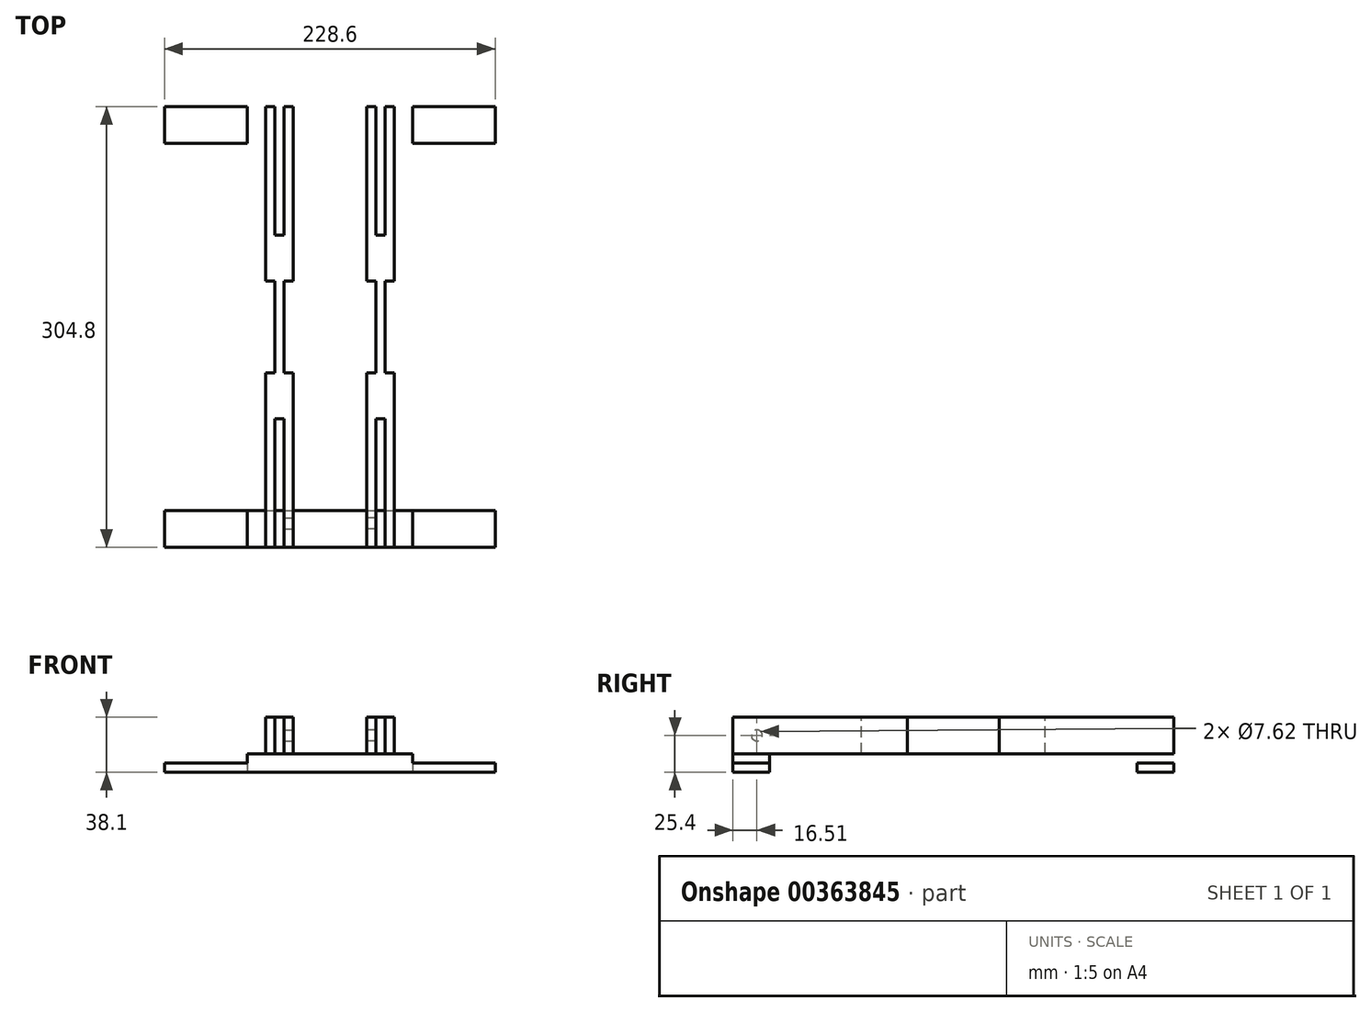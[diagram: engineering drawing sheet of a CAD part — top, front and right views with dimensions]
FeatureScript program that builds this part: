
annotation { "Feature Type Name" : "Feature", "Feature Type Description" : "" }
export const myFeature = defineFeature(function(context is Context, id is Id, definition is map)
    precondition{}
    {
        {
            var Q0;
            Q0=qCreatedBy(makeId("Top.planeOp"),FACE);
            var sketch = newSketch(context, id + "F0", { "sketchPlane" : qUnion([Q0])});
            skLineSegment(sketch, "E0.bottom", {"start": v(-114.3, 152.4) * mm, "end": v(114.3, 152.4) * mm});
            skLineSegment(sketch, "E0.top", {"start": v(-114.3, 127) * mm, "end": v(114.3, 127) * mm});
            skLineSegment(sketch, "E0.left", {"start": v(-114.3, 152.4) * mm, "end": v(-114.3, 127) * mm});
            skLineSegment(sketch, "E0.right", {"start": v(114.3, 152.4) * mm, "end": v(114.3, 127) * mm});
            skLineSegment(sketch, "E1", {"start": v(-113.97, 0) * mm, "end": v(125.77, 0) * mm});
            skLineSegment(sketch, "E2.MirrorCS", {"start": v(-114.3, -152.4) * mm, "end": v(114.3, -152.4) * mm});
            skLineSegment(sketch, "E3.MirrorCS", {"start": v(-114.3, -152.4) * mm, "end": v(-114.3, -127) * mm});
            skLineSegment(sketch, "E4.MirrorCS", {"start": v(-114.3, -127) * mm, "end": v(114.3, -127) * mm});
            skLineSegment(sketch, "E5.MirrorCS", {"start": v(114.3, -152.4) * mm, "end": v(114.3, -127) * mm});
            skLineSegment(sketch, "E6.bottom", {"start": v(-57.15, 152.4) * mm, "end": v(57.15, 152.4) * mm});
            skLineSegment(sketch, "E6.top", {"start": v(-57.15, 127) * mm, "end": v(57.15, 127) * mm});
            skLineSegment(sketch, "E6.left", {"start": v(-57.15, 152.4) * mm, "end": v(-57.15, 127) * mm});
            skLineSegment(sketch, "E6.right", {"start": v(57.15, 152.4) * mm, "end": v(57.15, 127) * mm});
            skLineSegment(sketch, "E7.MirrorCS", {"start": v(-57.15, -127) * mm, "end": v(57.15, -127) * mm});
            skLineSegment(sketch, "E8.MirrorCS", {"start": v(-57.15, -152.4) * mm, "end": v(-57.15, -127) * mm});
            skLineSegment(sketch, "E9.MirrorCS", {"start": v(57.15, -152.4) * mm, "end": v(57.15, -127) * mm});
            skLineSegment(sketch, "E10.MirrorCS", {"start": v(-57.15, -152.4) * mm, "end": v(57.15, -152.4) * mm});
            skLineSegment(sketch, "E11", {"start": v(0, 0) * mm, "end": v(0, -127) * mm});
            skSolve(sketch);
        }
        {
            var Q0;
            {var subQ0=sQuery(id+"F0.wireOp",EDGE,"E5.MirrorCS");Q0=makeQuery(id+"F0.imprint","IMPRINT",FACE,{"disambiguationData":[TD([[makeQuery(id+"F0.imprint","IMPRINT",EDGE,{"derivedFrom":subQ0}),1.0]])]});}
            var Q1;
            {var subQ0=sQuery(id+"F0.wireOp",EDGE,"E3.MirrorCS");Q1=makeQuery(id+"F0.imprint","IMPRINT",FACE,{"disambiguationData":[TD([[makeQuery(id+"F0.imprint","IMPRINT",EDGE,{"derivedFrom":subQ0}),-1.0]])]});}
            var Q2;
            {var subQ0=sQuery(id+"F0.wireOp",EDGE,"E0.left");Q2=makeQuery(id+"F0.imprint","IMPRINT",FACE,{"disambiguationData":[TD([[makeQuery(id+"F0.imprint","IMPRINT",EDGE,{"derivedFrom":subQ0}),1.0]])]});}
            var Q3;
            {var subQ0=sQuery(id+"F0.wireOp",EDGE,"E0.right");Q3=makeQuery(id+"F0.imprint","IMPRINT",FACE,{"disambiguationData":[TD([[makeQuery(id+"F0.imprint","IMPRINT",EDGE,{"derivedFrom":subQ0}),-1.0]])]});}
            extrude(context, id + "F1", {"entities" : qUnion([Q0, Q1, Q2, Q3]), "depth" : 6.35 * mm});
        }
        {
            var Q0;
            Q0=makeQuery(id+"F0.imprint","IMPRINT",FACE,{"disambiguationData":[TD([[makeQuery(id+"F0.imprint","IMPRINT",EDGE,{"derivedFrom":sQuery(id+"F0.wireOp",EDGE,"E8.MirrorCS")}),-1.0]])]});
            var Q1;
            Q1=makeQuery(id+"F0.imprint","IMPRINT",FACE,{"disambiguationData":[TD([[makeQuery(id+"F0.imprint","IMPRINT",EDGE,{"derivedFrom":sQuery(id+"F0.wireOp",EDGE,"E6.bottom")}),-1.0]])]});
            extrude(context, id + "F2", {"entities" : qUnion([Q0, Q1]), "depth" : 12.7 * mm});
        }
        {
            var Q0;
            Q0=makeQuery(id+"F1.opExtrude","SWEPT_BODY",BODY,{"disambiguationData":[OSD([sQuery(id+"F0.wireOp",EDGE,"E0.bottom"),sQuery(id+"F0.wireOp",EDGE,"E0.top"),sQuery(id+"F0.wireOp",EDGE,"E0.left"),sQuery(id+"F0.wireOp",EDGE,"E6.left")])]});
            var Q1;
            Q1=makeQuery(id+"F1.opExtrude","SWEPT_BODY",BODY,{"disambiguationData":[OSD([sQuery(id+"F0.wireOp",EDGE,"E0.bottom"),sQuery(id+"F0.wireOp",EDGE,"E0.top"),sQuery(id+"F0.wireOp",EDGE,"E0.right"),sQuery(id+"F0.wireOp",EDGE,"E6.right")])]});
            var Q2;
            Q2=makeQuery(id+"F1.opExtrude","SWEPT_BODY",BODY,{"disambiguationData":[OSD([sQuery(id+"F0.wireOp",EDGE,"E2.MirrorCS"),sQuery(id+"F0.wireOp",EDGE,"E3.MirrorCS"),sQuery(id+"F0.wireOp",EDGE,"E4.MirrorCS"),sQuery(id+"F0.wireOp",EDGE,"E8.MirrorCS")])]});
            var Q3;
            Q3=makeQuery(id+"F1.opExtrude","SWEPT_BODY",BODY,{"disambiguationData":[OSD([sQuery(id+"F0.wireOp",EDGE,"E2.MirrorCS"),sQuery(id+"F0.wireOp",EDGE,"E4.MirrorCS"),sQuery(id+"F0.wireOp",EDGE,"E5.MirrorCS"),sQuery(id+"F0.wireOp",EDGE,"E9.MirrorCS")])]});
            var Q4;
            Q4=makeQuery(id+"F2.opExtrude","SWEPT_BODY",BODY,{"disambiguationData":[OSD([sQuery(id+"F0.wireOp",EDGE,"E6.bottom"),sQuery(id+"F0.wireOp",EDGE,"E6.top"),sQuery(id+"F0.wireOp",EDGE,"E6.left"),sQuery(id+"F0.wireOp",EDGE,"E6.right")])]});
            var Q5;
            Q5=makeQuery(id+"F2.opExtrude","SWEPT_BODY",BODY,{"disambiguationData":[OSD([sQuery(id+"F0.wireOp",EDGE,"E8.MirrorCS"),sQuery(id+"F0.wireOp",EDGE,"E9.MirrorCS"),sQuery(id+"F0.wireOp",EDGE,"E10.MirrorCS"),sQuery(id+"F0.wireOp",EDGE,"E7.MirrorCS")])]});
            booleanBodies(context, id + "F3", {"operationType" : BooleanOperationType.UNION, "tools" : qUnion([Q0, Q1, Q2, Q3, Q4, Q5])});
        }
        {
            var Q0;
            {var subQ0=sQuery(id+"F0.wireOp",EDGE,"E10.MirrorCS");var subQ1=sQuery(id+"F0.wireOp",EDGE,"E2.MirrorCS");Q0=makeQuery(id+"F3.opBoolean","MERGE",FACE,{"derivedFrom":[makeQuery(id+"F1.opExtrude","SWEPT_FACE",FACE,{"disambiguationData":[OSD([subQ1]),TDD([makeQuery(id+"F0.imprint","IMPRINT",EDGE,{"disambiguationData":[TD([[makeQuery(id+"F0.imprint","INTERSECT",VERTEX,{"derivedFrom":[subQ1,sQuery(id+"F0.wireOp",EDGE,"E3.MirrorCS")]}),-1.0]])],"derivedFrom":subQ1})])]}),makeQuery(id+"F1.opExtrude","SWEPT_FACE",FACE,{"disambiguationData":[OSD([subQ1]),TDD([makeQuery(id+"F0.imprint","IMPRINT",EDGE,{"disambiguationData":[TD([[makeQuery(id+"F0.imprint","INTERSECT",VERTEX,{"derivedFrom":[subQ1,sQuery(id+"F0.wireOp",EDGE,"E5.MirrorCS")]}),1.0]])],"derivedFrom":subQ1})])]}),makeQuery(id+"F2.opExtrude","SWEPT_FACE",FACE,{"disambiguationData":[OSD([subQ0])]})]});}
            var sketch = newSketch(context, id + "F4", { "sketchPlane" : qUnion([Q0])});
            skLineSegment(sketch, "E12", {"start": v(0, 59.29) * mm, "end": v(0, 0) * mm});
            skLineSegment(sketch, "E13.bottom", {"start": v(-44.45, 12.7) * mm, "end": v(-38.1, 12.7) * mm});
            skLineSegment(sketch, "E13.top", {"start": v(-44.45, 38.1) * mm, "end": v(-38.1, 38.1) * mm});
            skLineSegment(sketch, "E13.left", {"start": v(-44.45, 12.7) * mm, "end": v(-44.45, 38.1) * mm});
            skLineSegment(sketch, "E13.right", {"start": v(-38.1, 12.7) * mm, "end": v(-38.1, 38.1) * mm});
            skLineSegment(sketch, "E14.bottom", {"start": v(-31.75, 12.7) * mm, "end": v(-25.4, 12.7) * mm});
            skLineSegment(sketch, "E14.top", {"start": v(-31.75, 38.1) * mm, "end": v(-25.4, 38.1) * mm});
            skLineSegment(sketch, "E14.left", {"start": v(-31.75, 12.7) * mm, "end": v(-31.75, 38.1) * mm});
            skLineSegment(sketch, "E14.right", {"start": v(-25.4, 12.7) * mm, "end": v(-25.4, 38.1) * mm});
            skLineSegment(sketch, "E15.MirrorCS", {"start": v(25.4, 12.7) * mm, "end": v(25.4, 38.1) * mm});
            skLineSegment(sketch, "E16.MirrorCS", {"start": v(31.75, 38.1) * mm, "end": v(25.4, 38.1) * mm});
            skLineSegment(sketch, "E17.MirrorCS", {"start": v(31.75, 12.7) * mm, "end": v(25.4, 12.7) * mm});
            skLineSegment(sketch, "E18.MirrorCS", {"start": v(31.75, 12.7) * mm, "end": v(31.75, 38.1) * mm});
            skLineSegment(sketch, "E19.MirrorCS", {"start": v(38.1, 12.7) * mm, "end": v(38.1, 38.1) * mm});
            skLineSegment(sketch, "E20.MirrorCS", {"start": v(44.45, 12.7) * mm, "end": v(44.45, 38.1) * mm});
            skLineSegment(sketch, "E21.MirrorCS", {"start": v(44.45, 38.1) * mm, "end": v(38.1, 38.1) * mm});
            skLineSegment(sketch, "E22.MirrorCS", {"start": v(44.45, 12.7) * mm, "end": v(38.1, 12.7) * mm});
            skLineSegment(sketch, "E23.bottom", {"start": v(-38.1, 38.1) * mm, "end": v(-31.75, 38.1) * mm});
            skLineSegment(sketch, "E23.top", {"start": v(-38.1, 12.7) * mm, "end": v(-31.75, 12.7) * mm});
            skLineSegment(sketch, "E23.left", {"start": v(-38.1, 38.1) * mm, "end": v(-38.1, 12.7) * mm});
            skLineSegment(sketch, "E23.right", {"start": v(-31.75, 38.1) * mm, "end": v(-31.75, 12.7) * mm});
            skLineSegment(sketch, "E24.bottom", {"start": v(31.75, 38.1) * mm, "end": v(38.1, 38.1) * mm});
            skLineSegment(sketch, "E24.top", {"start": v(31.75, 12.7) * mm, "end": v(38.1, 12.7) * mm});
            skLineSegment(sketch, "E24.left", {"start": v(31.75, 38.1) * mm, "end": v(31.75, 12.7) * mm});
            skLineSegment(sketch, "E24.right", {"start": v(38.1, 38.1) * mm, "end": v(38.1, 12.7) * mm});
            skSolve(sketch);
        }
        {
            var Q0;
            Q0=makeQuery(id+"F4.imprint","IMPRINT",FACE,{"disambiguationData":[TD([[makeQuery(id+"F4.imprint","IMPRINT",EDGE,{"derivedFrom":sQuery(id+"F4.wireOp",EDGE,"E13.bottom")}),1.0]])]});
            var Q1;
            Q1=makeQuery(id+"F4.imprint","IMPRINT",FACE,{"disambiguationData":[TD([[makeQuery(id+"F4.imprint","IMPRINT",EDGE,{"derivedFrom":sQuery(id+"F4.wireOp",EDGE,"E14.bottom")}),1.0]])]});
            var Q2;
            Q2=makeQuery(id+"F4.imprint","IMPRINT",FACE,{"disambiguationData":[TD([[makeQuery(id+"F4.imprint","IMPRINT",EDGE,{"derivedFrom":sQuery(id+"F4.wireOp",EDGE,"E19.MirrorCS")}),-1.0]])]});
            var Q3;
            Q3=makeQuery(id+"F4.imprint","IMPRINT",FACE,{"disambiguationData":[TD([[makeQuery(id+"F4.imprint","IMPRINT",EDGE,{"derivedFrom":sQuery(id+"F4.wireOp",EDGE,"E23.bottom")}),-1.0]])]});
            var Q4;
            Q4=makeQuery(id+"F4.imprint","IMPRINT",FACE,{"disambiguationData":[TD([[makeQuery(id+"F4.imprint","IMPRINT",EDGE,{"derivedFrom":sQuery(id+"F4.wireOp",EDGE,"E15.MirrorCS")}),-1.0]])]});
            var Q5;
            Q5=makeQuery(id+"F4.imprint","IMPRINT",FACE,{"disambiguationData":[TD([[makeQuery(id+"F4.imprint","IMPRINT",EDGE,{"derivedFrom":sQuery(id+"F4.wireOp",EDGE,"E24.bottom")}),-1.0]])]});
            var Q6;
            Q6=makeQuery(id+"F4.imprint","IMPRINT",FACE,{"disambiguationData":[TD([[makeQuery(id+"F4.imprint","IMPRINT",EDGE,{"derivedFrom":sQuery(id+"F4.wireOp",EDGE,"E20.MirrorCS")}),1.0]])]});
            extrude(context, id + "F5", {"entities" : qUnion([Q0, Q1, Q2, Q3, Q4, Q5, Q6]), "oppositeDirection" : true, "depth" : 304.8 * mm});
        }
        {
            var Q0;
            Q0=makeQuery(id+"F5.opExtrude","SWEPT_FACE",FACE,{"disambiguationData":[OSD([sQuery(id+"F4.wireOp",EDGE,"E13.left")])]});
            var sketch = newSketch(context, id + "F6", { "sketchPlane" : qUnion([Q0])});
            skLineSegment(sketch, "E25.bottom", {"start": v(-31.75, 12.7) * mm, "end": v(31.75, 12.7) * mm});
            skLineSegment(sketch, "E25.top", {"start": v(-31.75, 38.1) * mm, "end": v(31.75, 38.1) * mm});
            skLineSegment(sketch, "E25.left", {"start": v(-31.75, 12.7) * mm, "end": v(-31.75, 38.1) * mm});
            skLineSegment(sketch, "E25.right", {"start": v(31.75, 12.7) * mm, "end": v(31.75, 38.1) * mm});
            skSolve(sketch);
        }
        {
            var Q0;
            Q0=makeQuery(id+"F6.imprint","IMPRINT",FACE,{"disambiguationData":[TD([[makeQuery(id+"F6.imprint","IMPRINT",EDGE,{"derivedFrom":sQuery(id+"F6.wireOp",EDGE,"E25.bottom")}),1.0]])]});
            extrude(context, id + "F7", {"entities" : qUnion([Q0]), "operationType" : NewBodyOperationType.REMOVE, "oppositeDirection" : true, "depth" : 6.35 * mm});
        }
        {
            var Q0;
            Q0=makeQuery(id+"F5.opExtrude","SWEPT_FACE",FACE,{"disambiguationData":[OSD([sQuery(id+"F4.wireOp",EDGE,"E14.right")])]});
            var sketch = newSketch(context, id + "F8", { "sketchPlane" : qUnion([Q0])});
            skLineSegment(sketch, "E26.bottom", {"start": v(-31.75, 38.1) * mm, "end": v(31.75, 38.1) * mm});
            skLineSegment(sketch, "E26.top", {"start": v(-31.75, 12.7) * mm, "end": v(31.75, 12.7) * mm});
            skLineSegment(sketch, "E26.left", {"start": v(-31.75, 38.1) * mm, "end": v(-31.75, 12.7) * mm});
            skLineSegment(sketch, "E26.right", {"start": v(31.75, 38.1) * mm, "end": v(31.75, 12.7) * mm});
            skSolve(sketch);
        }
        {
            var Q0;
            Q0 = qSketchRegion(id + "F8", true);
            extrude(context, id + "F9", {"entities" : qUnion([Q0]), "operationType" : NewBodyOperationType.REMOVE, "oppositeDirection" : true, "depth" : 6.35 * mm});
        }
        {
            var Q0;
            Q0=makeQuery(id+"F5.opExtrude","SWEPT_FACE",FACE,{"disambiguationData":[OSD([sQuery(id+"F4.wireOp",EDGE,"E20.MirrorCS")])]});
            var sketch = newSketch(context, id + "F10", { "sketchPlane" : qUnion([Q0])});
            skLineSegment(sketch, "E27.bottom", {"start": v(-31.75, 38.1) * mm, "end": v(31.75, 38.1) * mm});
            skLineSegment(sketch, "E27.top", {"start": v(-31.75, 12.7) * mm, "end": v(31.75, 12.7) * mm});
            skLineSegment(sketch, "E27.left", {"start": v(-31.75, 38.1) * mm, "end": v(-31.75, 12.7) * mm});
            skLineSegment(sketch, "E27.right", {"start": v(31.75, 38.1) * mm, "end": v(31.75, 12.7) * mm});
            skSolve(sketch);
        }
        {
            var Q0;
            Q0=makeQuery(id+"F10.imprint","IMPRINT",FACE,{"disambiguationData":[TD([[makeQuery(id+"F10.imprint","IMPRINT",EDGE,{"derivedFrom":sQuery(id+"F10.wireOp",EDGE,"E27.bottom")}),1.0]])]});
            extrude(context, id + "F11", {"entities" : qUnion([Q0]), "operationType" : NewBodyOperationType.REMOVE, "oppositeDirection" : true, "depth" : 6.35 * mm});
        }
        {
            var Q0;
            Q0=makeQuery(id+"F5.opExtrude","SWEPT_FACE",FACE,{"disambiguationData":[OSD([sQuery(id+"F4.wireOp",EDGE,"E15.MirrorCS")])]});
            var sketch = newSketch(context, id + "F12", { "sketchPlane" : qUnion([Q0])});
            skLineSegment(sketch, "E28.bottom", {"start": v(-31.75, 38.1) * mm, "end": v(31.75, 38.1) * mm});
            skLineSegment(sketch, "E28.top", {"start": v(-31.75, 12.7) * mm, "end": v(31.75, 12.7) * mm});
            skLineSegment(sketch, "E28.left", {"start": v(-31.75, 38.1) * mm, "end": v(-31.75, 12.7) * mm});
            skLineSegment(sketch, "E28.right", {"start": v(31.75, 38.1) * mm, "end": v(31.75, 12.7) * mm});
            skSolve(sketch);
        }
        {
            var Q0;
            Q0 = qSketchRegion(id + "F12", true);
            extrude(context, id + "F13", {"entities" : qUnion([Q0]), "operationType" : NewBodyOperationType.REMOVE, "oppositeDirection" : true, "depth" : 6.35 * mm});
        }
        {
            var Q0;
            Q0=makeQuery(id+"F5.opExtrude","SWEPT_FACE",FACE,{"disambiguationData":[OSD([sQuery(id+"F4.wireOp",EDGE,"E13.top"),sQuery(id+"F4.wireOp",EDGE,"E14.top"),sQuery(id+"F4.wireOp",EDGE,"E23.bottom")])]});
            var sketch = newSketch(context, id + "F14", { "sketchPlane" : qUnion([Q0])});
            skLineSegment(sketch, "E29", {"start": v(0, 158.09) * mm, "end": v(0, -156.8) * mm});
            skLineSegment(sketch, "E30.bottom", {"start": v(-38.1, 63.5) * mm, "end": v(-31.75, 63.5) * mm});
            skLineSegment(sketch, "E30.top", {"start": v(-38.1, 152.4) * mm, "end": v(-31.75, 152.4) * mm});
            skLineSegment(sketch, "E30.left", {"start": v(-38.1, 63.5) * mm, "end": v(-38.1, 152.4) * mm});
            skLineSegment(sketch, "E30.right", {"start": v(-31.75, 63.5) * mm, "end": v(-31.75, 152.4) * mm});
            skLineSegment(sketch, "E31", {"start": v(-107.54, 0) * mm, "end": v(83.71, 0) * mm});
            skLineSegment(sketch, "E32.MirrorCS", {"start": v(-31.75, -63.5) * mm, "end": v(-31.75, -152.4) * mm});
            skLineSegment(sketch, "E33.MirrorCS", {"start": v(-38.1, -63.5) * mm, "end": v(-38.1, -152.4) * mm});
            skLineSegment(sketch, "E34", {"start": v(-38.1, -63.5) * mm, "end": v(-31.75, -63.5) * mm});
            skLineSegment(sketch, "E35", {"start": v(-31.75, -152.4) * mm, "end": v(-38.1, -152.4) * mm});
            skLineSegment(sketch, "E36.MirrorCS", {"start": v(38.1, 63.5) * mm, "end": v(38.1, 152.4) * mm});
            skLineSegment(sketch, "E37.MirrorCS", {"start": v(31.75, 63.5) * mm, "end": v(31.75, 152.4) * mm});
            skLineSegment(sketch, "E38.MirrorCS", {"start": v(38.1, -63.5) * mm, "end": v(38.1, -152.4) * mm});
            skLineSegment(sketch, "E39.MirrorCS", {"start": v(31.75, -63.5) * mm, "end": v(31.75, -152.4) * mm});
            skLineSegment(sketch, "E40", {"start": v(31.75, 152.4) * mm, "end": v(38.1, 152.4) * mm});
            skLineSegment(sketch, "E41", {"start": v(31.75, 63.5) * mm, "end": v(38.1, 63.5) * mm});
            skLineSegment(sketch, "E42", {"start": v(31.75, -63.5) * mm, "end": v(38.1, -63.5) * mm});
            skLineSegment(sketch, "E43", {"start": v(31.75, -152.4) * mm, "end": v(38.1, -152.4) * mm});
            skSolve(sketch);
        }
        {
            var Q0;
            Q0 = qSketchRegion(id + "F14", true);
            extrude(context, id + "F15", {"entities" : qUnion([Q0]), "operationType" : NewBodyOperationType.REMOVE, "oppositeDirection" : true, "depth" : 25.4 * mm});
        }
        {
            var Q0;
            {var subQ2=sQuery(id+"F4.wireOp",EDGE,"E14.right");Q0=makeQuery(id+"F9.boolean.opBoolean","SPLIT",FACE,{"disambiguationData":[TD([makeQuery(id+"F9.opExtrude","SWEPT_FACE",FACE,{"disambiguationData":[OSD([sQuery(id+"F8.wireOp",EDGE,"E26.left")])]})])],"derivedFrom":makeQuery(id+"F5.opExtrude","SWEPT_FACE",FACE,{"disambiguationData":[OSD([subQ2])]})});}
            var sketch = newSketch(context, id + "F16", { "sketchPlane" : qUnion([Q0])});
            skCircle(sketch, "E44", {"center": v(-135.9, 25.4) * mm, "radius": 3.81 * mm});
            skSolve(sketch);
        }
        {
            var Q0;
            Q0 = qSketchRegion(id + "F16", true);
            extrude(context, id + "F17", {"entities" : qUnion([Q0]), "operationType" : NewBodyOperationType.REMOVE, "oppositeDirection" : true, "depth" : 6.35 * mm});
        }
        {
            var Q0;
            {var subQ6=sQuery(id+"F4.wireOp",EDGE,"E15.MirrorCS");Q0=makeQuery(id+"F13.boolean.opBoolean","SPLIT",FACE,{"disambiguationData":[TD([makeQuery(id+"F13.opExtrude","SWEPT_FACE",FACE,{"disambiguationData":[OSD([sQuery(id+"F12.wireOp",EDGE,"E28.right")])]})])],"derivedFrom":makeQuery(id+"F5.opExtrude","SWEPT_FACE",FACE,{"disambiguationData":[OSD([subQ6])]})});}
            var sketch = newSketch(context, id + "F18", { "sketchPlane" : qUnion([Q0])});
            skCircle(sketch, "E45", {"center": v(135.89, 25.4) * mm, "radius": 3.81 * mm});
            skSolve(sketch);
        }
        {
            var Q0;
            Q0 = qSketchRegion(id + "F18", true);
            extrude(context, id + "F19", {"entities" : qUnion([Q0]), "operationType" : NewBodyOperationType.REMOVE, "oppositeDirection" : true, "depth" : 6.35 * mm});
        }
    });
